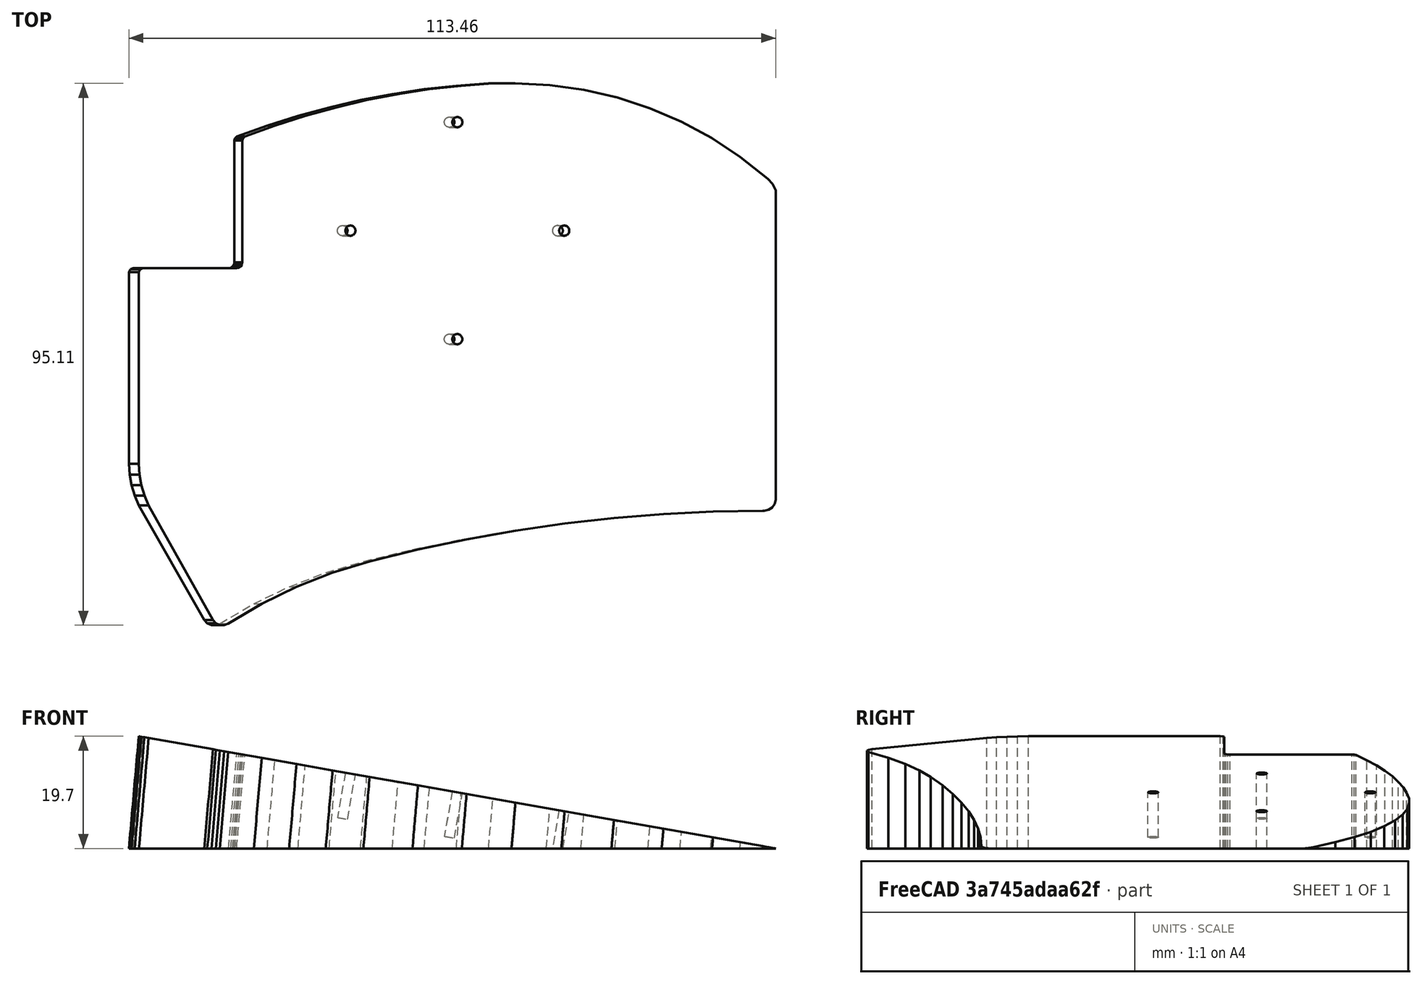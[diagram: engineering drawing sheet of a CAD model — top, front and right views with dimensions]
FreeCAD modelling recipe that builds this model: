
FCSTD DOCUMENT  (FreeCAD 1.0R39319 (Git))
Label: ferris_sweep_wedge
License: All rights reserved
LicenseURL: http://en.wikipedia.org/wiki/All_rights_reserved
objects: Sketcher::SketchObject×3, PartDesign::Plane×1, PartDesign::AdditiveLoft×1, PartDesign::Pocket×1, PartDesign::Body×1
note: 14 computed .brp shape members not serialized (recipe doc carries the construction recipe); baked Part::Feature solids carry a one-line shape summary decoded from their .brp

FEATURE [Sketcher::SketchObject] Sketch001  label="Bottom"
  ArcFitTolerance = 0
  AttachmentSupport = -> [XY_Plane]
  FullyConstrained = false
  MakeInternals = false
  MapMode = 5
  sketch-geometry (59):
    g0: LineSegment StartX=-2.031 StartY=-29.0839 StartZ=0 EndX=-1.25795 EndY=-28.9437 EndZ=0
    g1: LineSegment StartX=-1.25795 StartY=-28.9437 StartZ=0 EndX=-0.618525 EndY=-28.5347 EndZ=0
    g2: LineSegment StartX=-0.618525 StartY=-28.5347 StartZ=0 EndX=-0.176591 EndY=-27.9176 EndZ=0
    g3: LineSegment StartX=-0.176591 StartY=-27.9176 StartZ=0 EndX=0.004 EndY=-27.153 EndZ=0
    g4: LineSegment StartX=0.004 StartY=-27.153 StartZ=0 EndX=-0.004 EndY=27.153 EndZ=0
    g5: LineSegment StartX=-0.004 StartY=27.153 StartZ=0 EndX=-0.560859 EndY=28.271 EndZ=0
    g6: LineSegment StartX=-0.560859 StartY=28.271 StartZ=0 EndX=-1.431 EndY=29.167 EndZ=0
    g7: LineSegment StartX=-1.431 StartY=29.167 StartZ=0 EndX=-6.27251 EndY=32.9898 EndZ=0
    g8: LineSegment StartX=-6.27251 StartY=32.9898 StartZ=0 EndX=-11.4055 EndY=36.3443 EndZ=0
    g9: LineSegment StartX=-11.4055 StartY=36.3443 StartZ=0 EndX=-16.7956 EndY=39.2176 EndZ=0
    g10: LineSegment StartX=-16.7956 StartY=39.2176 StartZ=0 EndX=-22.4087 EndY=41.5972 EndZ=0
    g11: LineSegment StartX=-22.4087 StartY=41.5972 StartZ=0 EndX=-28.2105 EndY=43.4702 EndZ=0
    g12: LineSegment StartX=-28.2105 StartY=43.4702 StartZ=0 EndX=-34.1668 EndY=44.8238 EndZ=0
    g13: LineSegment StartX=-34.1668 StartY=44.8238 StartZ=0 EndX=-40.2434 EndY=45.6453 EndZ=0
    g14: LineSegment StartX=-40.2434 StartY=45.6453 StartZ=0 EndX=-46.406 EndY=45.922 EndZ=0
    g15: LineSegment StartX=-46.406 StartY=45.922 StartZ=0 EndX=-50.381 EndY=45.924 EndZ=0
    g16: LineSegment StartX=-50.381 StartY=45.924 StartZ=0 EndX=-56.0425 EndY=45.5256 EndZ=0
    g17: LineSegment StartX=-56.0425 StartY=45.5256 StartZ=0 EndX=-61.6774 EndY=44.9052 EndZ=0
    g18: LineSegment StartX=-61.6774 StartY=44.9052 StartZ=0 EndX=-67.2792 EndY=44.0642 EndZ=0
    g19: LineSegment StartX=-67.2792 StartY=44.0642 StartZ=0 EndX=-72.8414 EndY=43.004 EndZ=0
    g20: LineSegment StartX=-72.8414 StartY=43.004 StartZ=0 EndX=-78.3576 EndY=41.7259 EndZ=0
    g21: LineSegment StartX=-78.3576 StartY=41.7259 StartZ=0 EndX=-83.8215 EndY=40.2313 EndZ=0
    g22: LineSegment StartX=-83.8215 StartY=40.2313 StartZ=0 EndX=-89.2264 EndY=38.5216 EndZ=0
    g23: LineSegment StartX=-89.2264 StartY=38.5216 StartZ=0 EndX=-94.566 EndY=36.598 EndZ=0
    g24: LineSegment StartX=-94.566 StartY=36.598 StartZ=0 EndX=-94.8831 EndY=36.3211 EndZ=0
    g25: LineSegment StartX=-94.8831 StartY=36.3211 StartZ=0 EndX=-95.001 EndY=35.917 EndZ=0
    g26: LineSegment StartX=-95.001 StartY=35.917 StartZ=0 EndX=-94.996 EndY=14.521 EndZ=0
    g27: LineSegment StartX=-94.996 StartY=14.521 StartZ=0 EndX=-95.0721 EndY=14.1383 EndZ=0
    g28: LineSegment StartX=-95.0721 StartY=14.1383 StartZ=0 EndX=-95.2889 EndY=13.8139 EndZ=0
    g29: LineSegment StartX=-95.2889 StartY=13.8139 StartZ=0 EndX=-95.6133 EndY=13.5971 EndZ=0
    g30: LineSegment StartX=-95.6133 StartY=13.5971 StartZ=0 EndX=-95.996 EndY=13.521 EndZ=0
    g31: LineSegment StartX=-95.996 StartY=13.521 StartZ=0 EndX=-112.7 EndY=13.524 EndZ=0
    g32: LineSegment StartX=-112.7 StartY=13.524 StartZ=0 EndX=-113.23 EndY=13.3043 EndZ=0
    g33: LineSegment StartX=-113.23 StartY=13.3043 StartZ=0 EndX=-113.45 EndY=12.774 EndZ=0
    g34: LineSegment StartX=-113.45 StartY=12.774 StartZ=0 EndX=-113.462 EndY=7.28 EndZ=0
    g35: LineSegment StartX=-113.462 StartY=7.28 StartZ=0 EndX=-113.45 EndY=-18.3385 EndZ=0
    g36: LineSegment StartX=-113.45 StartY=-18.3385 StartZ=0 EndX=-113.462 EndY=-20.858 EndZ=0
    g37: LineSegment StartX=-113.462 StartY=-20.858 StartZ=0 EndX=-113.34 EndY=-22.7546 EndZ=0
    g38: LineSegment StartX=-113.34 StartY=-22.7546 StartZ=0 EndX=-113.005 EndY=-24.6193 EndZ=0
    g39: LineSegment StartX=-113.005 StartY=-24.6193 StartZ=0 EndX=-112.463 EndY=-26.4344 EndZ=0
    g40: LineSegment StartX=-112.463 StartY=-26.4344 StartZ=0 EndX=-111.716 EndY=-28.1821 EndZ=0
    g41: LineSegment StartX=-111.716 StartY=-28.1821 StartZ=0 EndX=-100.248 EndY=-48.3093 EndZ=0
    g42: LineSegment StartX=-100.248 StartY=-48.3093 StartZ=0 EndX=-99.7146 EndY=-48.8685 EndZ=0
    g43: LineSegment StartX=-99.7146 StartY=-48.8685 StartZ=0 EndX=-99.007 EndY=-49.179 EndZ=0
    g44: LineSegment StartX=-99.007 StartY=-49.179 StartZ=0 EndX=-98.2343 EndY=-49.1929 EndZ=0
    g45: LineSegment StartX=-98.2343 StartY=-49.1929 StartZ=0 EndX=-97.516 EndY=-48.908 EndZ=0
    g46: LineSegment StartX=-97.516 StartY=-48.908 StartZ=0 EndX=-91.5608 EndY=-45.436 EndZ=0
    g47: LineSegment StartX=-91.5608 StartY=-45.436 StartZ=0 EndX=-85.3593 EndY=-42.4507 EndZ=0
    g48: LineSegment StartX=-85.3593 StartY=-42.4507 StartZ=0 EndX=-78.9411 EndY=-39.9652 EndZ=0
    g49: LineSegment StartX=-78.9411 StartY=-39.9652 StartZ=0 EndX=-72.336 EndY=-37.9923 EndZ=0
    g50: LineSegment StartX=-72.336 StartY=-37.9923 StartZ=0 EndX=-63.7274 EndY=-35.919 EndZ=0
    g51: LineSegment StartX=-63.7274 StartY=-35.919 StartZ=0 EndX=-55.0644 EndY=-34.1183 EndZ=0
    g52: LineSegment StartX=-55.0644 StartY=-34.1183 StartZ=0 EndX=-46.3534 EndY=-32.591 EndZ=0
    g53: LineSegment StartX=-46.3534 StartY=-32.591 StartZ=0 EndX=-37.6009 EndY=-31.3379 EndZ=0
    g54: LineSegment StartX=-37.6009 StartY=-31.3379 StartZ=0 EndX=-28.8135 EndY=-30.3599 EndZ=0
    g55: LineSegment StartX=-28.8135 StartY=-30.3599 StartZ=0 EndX=-19.9975 EndY=-29.6578 EndZ=0
    g56: LineSegment StartX=-19.9975 StartY=-29.6578 StartZ=0 EndX=-11.1595 EndY=-29.2324 EndZ=0
    g57: LineSegment StartX=-11.1595 StartY=-29.2324 StartZ=0 EndX=-2.306 EndY=-29.0846 EndZ=0
    g58: LineSegment StartX=-2.306 StartY=-29.0846 StartZ=0 EndX=-2.031 EndY=-29.0839 EndZ=0
  constraints (1):
    c: Coincident(g58,g0)
FEATURE [PartDesign::Plane] DatumPlane  label="PCB Surface"
  AttachmentOffset = pos=(0,0,0) rot=(0,1,0;0.174533rad)
  AttachmentSupport = -> [XY_Plane]
  Length = 168.532
  MapMode = 5
  Placement = pos=(0,0,0) rot=(0,1,0;0.174533rad)
  ResizeMode = 0
  Width = 118.608
FEATURE [Sketcher::SketchObject] Sketch
  ArcFitTolerance = 0
  AttachmentSupport = -> [DatumPlane]
  FullyConstrained = true
  MakeInternals = false
  MapMode = 5
  Placement = pos=(0,0,0) rot=(0,1,0;0.174533rad)
  sketch-geometry (4):
    g0: Circle CenterX=-75.7688 CenterY=20.0817 CenterZ=0 NormalX=0 NormalY=0 NormalZ=-1 AngleXU=0 Radius=0.9
    g1: Circle CenterX=-56.7188 CenterY=39.1317 CenterZ=0 NormalX=0 NormalY=0 NormalZ=-1 AngleXU=0 Radius=0.9
    g2: Circle CenterX=-37.676 CenterY=20.079 CenterZ=0 NormalX=0 NormalY=0 NormalZ=-1 AngleXU=0 Radius=0.9
    g3: Circle CenterX=-56.726 CenterY=1.029 CenterZ=0 NormalX=0 NormalY=0 NormalZ=-1 AngleXU=0 Radius=0.9
  constraints (12):
    c: Equal(g1,g0)
    c: Equal(g0,g3)
    c: Equal(g3,g2)
    c: DistanceX(g3) = -56.726
    c: DistanceY(g3) = 1.029
    c: DistanceX(g2) = -37.676
    c: DistanceY(g2) = 20.079
    c: DistanceX(g0) = -75.7688
    c: DistanceY(g0) = 20.0817
    c: DistanceX(g1) = -56.7188
    c: DistanceY(g1) = 39.1317
    c: Diameter(g1) = 1.8  'diameter'
FEATURE [Sketcher::SketchObject] Sketch002  label="Top"
  ArcFitTolerance = 0
  AttachmentSupport = -> [DatumPlane]
  FullyConstrained = false
  MakeInternals = false
  MapMode = 5
  Placement = pos=(0,0,0) rot=(0,1,0;0.174533rad)
  sketch-geometry (59):
    g0: LineSegment StartX=-2.031 StartY=-29.0839 StartZ=0 EndX=-1.25795 EndY=-28.9437 EndZ=0
    g1: LineSegment StartX=-1.25795 StartY=-28.9437 StartZ=0 EndX=-0.618525 EndY=-28.5347 EndZ=0
    g2: LineSegment StartX=-0.618525 StartY=-28.5347 StartZ=0 EndX=-0.176591 EndY=-27.9176 EndZ=0
    g3: LineSegment StartX=-0.176591 StartY=-27.9176 StartZ=0 EndX=0.004 EndY=-27.153 EndZ=0
    g4: LineSegment StartX=0.004 StartY=-27.153 StartZ=0 EndX=-0.004 EndY=27.153 EndZ=0
    g5: LineSegment StartX=-0.004 StartY=27.153 StartZ=0 EndX=-0.560859 EndY=28.271 EndZ=0
    g6: LineSegment StartX=-0.560859 StartY=28.271 StartZ=0 EndX=-1.431 EndY=29.167 EndZ=0
    g7: LineSegment StartX=-1.431 StartY=29.167 StartZ=0 EndX=-6.27251 EndY=32.9898 EndZ=0
    g8: LineSegment StartX=-6.27251 StartY=32.9898 StartZ=0 EndX=-11.4055 EndY=36.3443 EndZ=0
    g9: LineSegment StartX=-11.4055 StartY=36.3443 StartZ=0 EndX=-16.7956 EndY=39.2176 EndZ=0
    g10: LineSegment StartX=-16.7956 StartY=39.2176 StartZ=0 EndX=-22.4087 EndY=41.5972 EndZ=0
    g11: LineSegment StartX=-22.4087 StartY=41.5972 StartZ=0 EndX=-28.2105 EndY=43.4702 EndZ=0
    g12: LineSegment StartX=-28.2105 StartY=43.4702 StartZ=0 EndX=-34.1668 EndY=44.8238 EndZ=0
    g13: LineSegment StartX=-34.1668 StartY=44.8238 StartZ=0 EndX=-40.2434 EndY=45.6453 EndZ=0
    g14: LineSegment StartX=-40.2434 StartY=45.6453 StartZ=0 EndX=-46.406 EndY=45.922 EndZ=0
    g15: LineSegment StartX=-46.406 StartY=45.922 StartZ=0 EndX=-50.381 EndY=45.924 EndZ=0
    g16: LineSegment StartX=-50.381 StartY=45.924 StartZ=0 EndX=-56.0425 EndY=45.5256 EndZ=0
    g17: LineSegment StartX=-56.0425 StartY=45.5256 StartZ=0 EndX=-61.6774 EndY=44.9052 EndZ=0
    g18: LineSegment StartX=-61.6774 StartY=44.9052 StartZ=0 EndX=-67.2792 EndY=44.0642 EndZ=0
    g19: LineSegment StartX=-67.2792 StartY=44.0642 StartZ=0 EndX=-72.8414 EndY=43.004 EndZ=0
    g20: LineSegment StartX=-72.8414 StartY=43.004 StartZ=0 EndX=-78.3576 EndY=41.7259 EndZ=0
    g21: LineSegment StartX=-78.3576 StartY=41.7259 StartZ=0 EndX=-83.8215 EndY=40.2313 EndZ=0
    g22: LineSegment StartX=-83.8215 StartY=40.2313 StartZ=0 EndX=-89.2264 EndY=38.5216 EndZ=0
    g23: LineSegment StartX=-89.2264 StartY=38.5216 StartZ=0 EndX=-94.566 EndY=36.598 EndZ=0
    g24: LineSegment StartX=-94.566 StartY=36.598 StartZ=0 EndX=-94.8831 EndY=36.3211 EndZ=0
    g25: LineSegment StartX=-94.8831 StartY=36.3211 StartZ=0 EndX=-95.001 EndY=35.917 EndZ=0
    g26: LineSegment StartX=-95.001 StartY=35.917 StartZ=0 EndX=-94.996 EndY=14.521 EndZ=0
    g27: LineSegment StartX=-94.996 StartY=14.521 StartZ=0 EndX=-95.0721 EndY=14.1383 EndZ=0
    g28: LineSegment StartX=-95.0721 StartY=14.1383 StartZ=0 EndX=-95.2889 EndY=13.8139 EndZ=0
    g29: LineSegment StartX=-95.2889 StartY=13.8139 StartZ=0 EndX=-95.6133 EndY=13.5971 EndZ=0
    g30: LineSegment StartX=-95.6133 StartY=13.5971 StartZ=0 EndX=-95.996 EndY=13.521 EndZ=0
    g31: LineSegment StartX=-95.996 StartY=13.521 StartZ=0 EndX=-112.7 EndY=13.524 EndZ=0
    g32: LineSegment StartX=-112.7 StartY=13.524 StartZ=0 EndX=-113.23 EndY=13.3043 EndZ=0
    g33: LineSegment StartX=-113.23 StartY=13.3043 StartZ=0 EndX=-113.45 EndY=12.774 EndZ=0
    g34: LineSegment StartX=-113.45 StartY=12.774 StartZ=0 EndX=-113.462 EndY=7.28 EndZ=0
    g35: LineSegment StartX=-113.462 StartY=7.28 StartZ=0 EndX=-113.45 EndY=-18.3385 EndZ=0
    g36: LineSegment StartX=-113.45 StartY=-18.3385 StartZ=0 EndX=-113.462 EndY=-20.858 EndZ=0
    g37: LineSegment StartX=-113.462 StartY=-20.858 StartZ=0 EndX=-113.34 EndY=-22.7546 EndZ=0
    g38: LineSegment StartX=-113.34 StartY=-22.7546 StartZ=0 EndX=-113.005 EndY=-24.6193 EndZ=0
    g39: LineSegment StartX=-113.005 StartY=-24.6193 StartZ=0 EndX=-112.463 EndY=-26.4344 EndZ=0
    g40: LineSegment StartX=-112.463 StartY=-26.4344 StartZ=0 EndX=-111.716 EndY=-28.1821 EndZ=0
    g41: LineSegment StartX=-111.716 StartY=-28.1821 StartZ=0 EndX=-100.248 EndY=-48.3093 EndZ=0
    g42: LineSegment StartX=-100.248 StartY=-48.3093 StartZ=0 EndX=-99.7146 EndY=-48.8685 EndZ=0
    g43: LineSegment StartX=-99.7146 StartY=-48.8685 StartZ=0 EndX=-99.007 EndY=-49.179 EndZ=0
    g44: LineSegment StartX=-99.007 StartY=-49.179 StartZ=0 EndX=-98.2343 EndY=-49.1929 EndZ=0
    g45: LineSegment StartX=-98.2343 StartY=-49.1929 StartZ=0 EndX=-97.516 EndY=-48.908 EndZ=0
    g46: LineSegment StartX=-97.516 StartY=-48.908 StartZ=0 EndX=-91.5608 EndY=-45.436 EndZ=0
    g47: LineSegment StartX=-91.5608 StartY=-45.436 StartZ=0 EndX=-85.3593 EndY=-42.4507 EndZ=0
    g48: LineSegment StartX=-85.3593 StartY=-42.4507 StartZ=0 EndX=-78.9411 EndY=-39.9652 EndZ=0
    g49: LineSegment StartX=-78.9411 StartY=-39.9652 StartZ=0 EndX=-72.336 EndY=-37.9923 EndZ=0
    g50: LineSegment StartX=-72.336 StartY=-37.9923 StartZ=0 EndX=-63.7274 EndY=-35.919 EndZ=0
    g51: LineSegment StartX=-63.7274 StartY=-35.919 StartZ=0 EndX=-55.0644 EndY=-34.1183 EndZ=0
    g52: LineSegment StartX=-55.0644 StartY=-34.1183 StartZ=0 EndX=-46.3534 EndY=-32.591 EndZ=0
    g53: LineSegment StartX=-46.3534 StartY=-32.591 StartZ=0 EndX=-37.6009 EndY=-31.3379 EndZ=0
    g54: LineSegment StartX=-37.6009 StartY=-31.3379 StartZ=0 EndX=-28.8135 EndY=-30.3599 EndZ=0
    g55: LineSegment StartX=-28.8135 StartY=-30.3599 StartZ=0 EndX=-19.9975 EndY=-29.6578 EndZ=0
    g56: LineSegment StartX=-19.9975 StartY=-29.6578 StartZ=0 EndX=-11.1595 EndY=-29.2324 EndZ=0
    g57: LineSegment StartX=-11.1595 StartY=-29.2324 StartZ=0 EndX=-2.306 EndY=-29.0846 EndZ=0
    g58: LineSegment StartX=-2.306 StartY=-29.0846 StartZ=0 EndX=-2.031 EndY=-29.0839 EndZ=0
  constraints (1):
    c: Coincident(g0,g58)
FEATURE [PartDesign::AdditiveLoft] AdditiveLoft  label="Block"
  Closed = false
  Profile = -> Sketch001
  Ruled = false
  Sections = -> [Sketch002]
  Suppressed = false
FEATURE [PartDesign::Pocket] Pocket  label="PCB Mounting Holes"
  BaseFeature = -> AdditiveLoft
  Direction = (-0.173648,0,-0.984808)
  Length = 8
  Length2 = 5
  Profile = -> Sketch
  ReferenceAxis = -> Sketch [N_Axis]
  Suppressed = false
  Type = 0
FEATURE [PartDesign::Body] Body
  AllowCompound = false
  Group = -> [Sketch001,Sketch002,DatumPlane,AdditiveLoft,Sketch,Pocket]
  Origin = -> Origin
  Tip = -> Pocket
